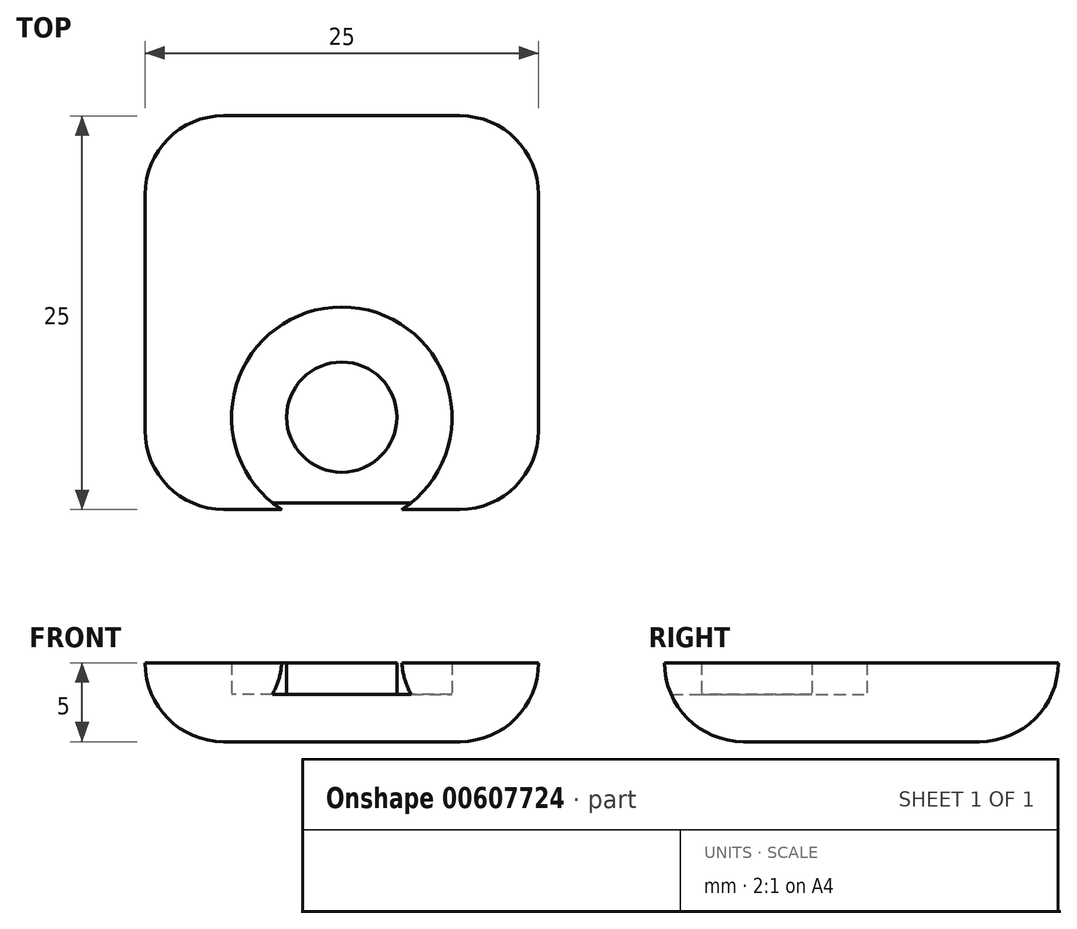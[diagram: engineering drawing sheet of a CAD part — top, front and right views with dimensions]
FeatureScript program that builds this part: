
annotation { "Feature Type Name" : "Feature", "Feature Type Description" : "" }
export const myFeature = defineFeature(function(context is Context, id is Id, definition is map)
    precondition{}
    {
        {
            var Q0;
            Q0=qCreatedBy(makeId("Top.planeOp"),FACE);
            var sketch = newSketch(context, id + "F0", { "sketchPlane" : qUnion([Q0])});
            skLineSegment(sketch, "E0", {"start": v(25, -11.86) * mm, "end": v(25, 13.14) * mm});
            skLineSegment(sketch, "E1", {"start": v(25, 13.14) * mm, "end": v(0, 13.14) * mm});
            skLineSegment(sketch, "E2", {"start": v(0, 13.14) * mm, "end": v(0, -11.86) * mm});
            skLineSegment(sketch, "E3", {"start": v(0, -11.86) * mm, "end": v(25, -11.86) * mm});
            skSolve(sketch);
        }
        {
            var Q0;
            Q0=makeQuery(id+"F0.imprint","IMPRINT",FACE,{"disambiguationData":[TD([[makeQuery(id+"F0.imprint","IMPRINT",EDGE,{"derivedFrom":sQuery(id+"F0.wireOp",EDGE,"E0")}),1.0]])]});
            extrude(context, id + "F1", {"entities" : qUnion([Q0]), "depth" : 5 * mm, "offsetDistance" : 25 * mm});
        }
        {
            var Q0;
            Q0=makeQuery(id+"F1.opExtrude","SWEPT_EDGE",EDGE,{"disambiguationData":[OSD([sQuery(id+"F0.wireOp",EDGE,"E1"),sQuery(id+"F0.wireOp",EDGE,"E2")])]});
            var Q1;
            Q1=makeQuery(id+"F1.opExtrude","SWEPT_EDGE",EDGE,{"disambiguationData":[OSD([sQuery(id+"F0.wireOp",EDGE,"E0"),sQuery(id+"F0.wireOp",EDGE,"E1")])]});
            var Q2;
            Q2=makeQuery(id+"F1.opExtrude","SWEPT_EDGE",EDGE,{"disambiguationData":[OSD([sQuery(id+"F0.wireOp",EDGE,"E2"),sQuery(id+"F0.wireOp",EDGE,"E3")])]});
            var Q3;
            Q3=makeQuery(id+"F1.opExtrude","SWEPT_EDGE",EDGE,{"disambiguationData":[OSD([sQuery(id+"F0.wireOp",EDGE,"E0"),sQuery(id+"F0.wireOp",EDGE,"E3")])]});
            fillet(context, id + "F2", {"entities" : qUnion([Q0, Q1, Q2, Q3]), "radius" : 5 * mm, "tangentPropagation" : true, "allowEdgeOverflow" : false});
        }
        {
            var Q0;
            Q0=makeQuery(id+"F1.opExtrude","CAP_EDGE",EDGE,{"disambiguationData":[OSD([sQuery(id+"F0.wireOp",EDGE,"E3")])],"isStart":true});
            var Q1;
            Q1=makeQuery(id+"F1.opExtrude","CAP_EDGE",EDGE,{"disambiguationData":[OSD([sQuery(id+"F0.wireOp",EDGE,"E2")])],"isStart":true});
            var Q2;
            Q2=makeQuery(id+"F1.opExtrude","CAP_EDGE",EDGE,{"disambiguationData":[OSD([sQuery(id+"F0.wireOp",EDGE,"E0")])],"isStart":true});
            var Q3;
            Q3=makeQuery(id+"F1.opExtrude","CAP_EDGE",EDGE,{"disambiguationData":[OSD([sQuery(id+"F0.wireOp",EDGE,"E1")])],"isStart":true});
            fillet(context, id + "F3", {"entities" : qUnion([Q0, Q1, Q2, Q3]), "radius" : 5 * mm, "tangentPropagation" : true, "allowEdgeOverflow" : false});
        }
        {
            var Q0;
            Q0=qCreatedBy(makeId("Top.planeOp"),FACE);
            var sketch = newSketch(context, id + "F4", { "sketchPlane" : qUnion([Q0])});
            skLineSegment(sketch, "E4.0.0", {"start": v(0, 8.14) * mm, "end": v(0, -6.86) * mm});
            skArc(sketch, "E4.0.1", {"start": v(0, -6.86) * mm, "mid": v(1.46, -10.4) * mm, "end": v(5, -11.86) * mm});
            skLineSegment(sketch, "E4.0.2", {"start": v(5, -11.86) * mm, "end": v(20, -11.86) * mm});
            skArc(sketch, "E4.0.3", {"start": v(20, -11.86) * mm, "mid": v(23.54, -10.4) * mm, "end": v(25, -6.86) * mm});
            skLineSegment(sketch, "E4.0.4", {"start": v(25, -6.86) * mm, "end": v(25, 8.14) * mm});
            skArc(sketch, "E4.0.5", {"start": v(25, 8.14) * mm, "mid": v(23.54, 11.68) * mm, "end": v(20, 13.14) * mm});
            skLineSegment(sketch, "E4.0.6", {"start": v(20, 13.14) * mm, "end": v(5, 13.14) * mm});
            skArc(sketch, "E4.0.7", {"start": v(5, 13.14) * mm, "mid": v(1.46, 11.68) * mm, "end": v(0, 8.14) * mm});
            skLineSegment(sketch, "E5", {"start": v(0, 0) * mm, "end": v(25, 0) * mm, "construction": true});
            skLineSegment(sketch, "E6", {"start": v(12.5, 13.14) * mm, "end": v(12.5, -11.86) * mm, "construction": true});
            skLineSegment(sketch, "E7", {"start": v(12.5, 0) * mm, "end": v(12.5, -6) * mm, "construction": true});
            skCircle(sketch, "E8", {"center": v(12.5, -6) * mm, "radius": 7 * mm});
            skCircle(sketch, "E9", {"center": v(12.5, -6) * mm, "radius": 3.5 * mm});
            skSolve(sketch);
        }
        {
            var Q0;
            Q0=makeQuery(id+"F4.imprint","IMPRINT",FACE,{"disambiguationData":[TD([[makeQuery(id+"F4.imprint","IMPRINT",EDGE,{"derivedFrom":sQuery(id+"F4.wireOp",EDGE,"E9")}),-1.0]])]});
            extrude(context, id + "F5", {"entities" : qUnion([Q0]), "operationType" : NewBodyOperationType.REMOVE, "depth" : 25 * mm, "offsetDistance" : 25 * mm, "hasSecondDirection" : true, "secondDirectionOppositeDirection" : false, "secondDirectionDepth" : 3 * mm});
        }
    });
